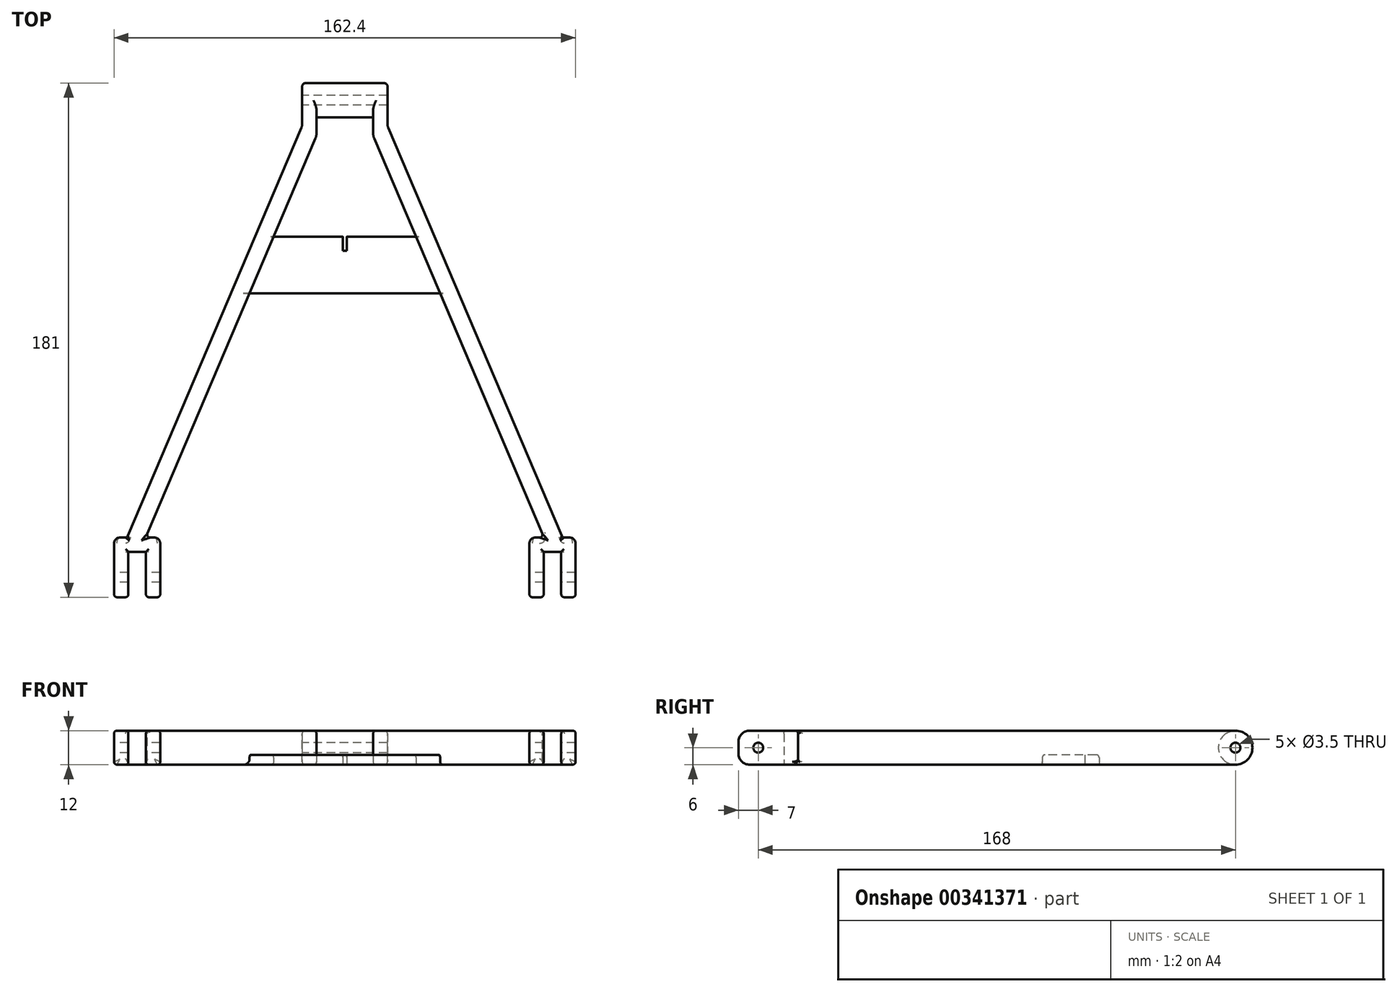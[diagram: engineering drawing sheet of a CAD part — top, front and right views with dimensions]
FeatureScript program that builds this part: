
annotation { "Feature Type Name" : "Feature", "Feature Type Description" : "" }
export const myFeature = defineFeature(function(context is Context, id is Id, definition is map)
    precondition{}
    {
        {
            var Q0;
            Q0=qCreatedBy(makeId("Top.planeOp"),FACE);
            var sketch = newSketch(context, id + "F0", { "sketchPlane" : qUnion([Q0])});
            skLineSegment(sketch, "E0.bottom", {"start": v(-15, 50) * mm, "end": v(-10, 50) * mm});
            skLineSegment(sketch, "E0.left", {"start": v(-15, 50) * mm, "end": v(-15, 35) * mm});
            skLineSegment(sketch, "E0.right", {"start": v(-10, 50) * mm, "end": v(-10, 31.42) * mm});
            skLineSegment(sketch, "E1", {"start": v(-15, 35) * mm, "end": v(-76.6, -110) * mm});
            skLineSegment(sketch, "E2", {"start": v(-10, 31.42) * mm, "end": v(-70.08, -110) * mm});
            skLineSegment(sketch, "E3.bottom", {"start": v(-81.2, -110) * mm, "end": v(-76.6, -110) * mm});
            skLineSegment(sketch, "E3.top", {"start": v(-76.2, -115) * mm, "end": v(-70, -115) * mm});
            skLineSegment(sketch, "E3.left", {"start": v(-81.2, -110) * mm, "end": v(-81.2, -115) * mm});
            skLineSegment(sketch, "E3.right", {"start": v(-65, -110) * mm, "end": v(-65, -115) * mm});
            skLineSegment(sketch, "E4.top", {"start": v(-65, -131) * mm, "end": v(-70, -131) * mm});
            skLineSegment(sketch, "E4.left", {"start": v(-65, -115) * mm, "end": v(-65, -131) * mm});
            skLineSegment(sketch, "E4.right", {"start": v(-70, -115) * mm, "end": v(-70, -131) * mm});
            skLineSegment(sketch, "E5.top", {"start": v(-81.2, -131) * mm, "end": v(-76.2, -131) * mm});
            skLineSegment(sketch, "E5.left", {"start": v(-81.2, -115) * mm, "end": v(-81.2, -131) * mm});
            skLineSegment(sketch, "E5.right", {"start": v(-76.2, -115) * mm, "end": v(-76.2, -131) * mm});
            skPoint(sketch, "E6", {"position": v(-73.1, -110) * mm});
            skLineSegment(sketch, "E7.trimOffspring", {"start": v(-70.08, -110) * mm, "end": v(-65, -110) * mm});
            skPoint(sketch, "E8.visualSharp", {"position": v(-76.6, -110) * mm});
            skPoint(sketch, "E9.visualSharp", {"position": v(-70.08, -110) * mm});
            skPoint(sketch, "E10.visualSharp", {"position": v(-81.2, -110) * mm});
            skPoint(sketch, "E11.visualSharp", {"position": v(-65, -110) * mm});
            skLineSegment(sketch, "E12", {"start": v(-25.05, -4) * mm, "end": v(-0.75, -4) * mm});
            skLineSegment(sketch, "E13", {"start": v(-33.55, -24) * mm, "end": v(0, -24) * mm});
            skLineSegment(sketch, "E14.MirrorCS", {"start": v(70.08, -110) * mm, "end": v(65, -110) * mm});
            skLineSegment(sketch, "E15.MirrorCS", {"start": v(81.2, -110) * mm, "end": v(76.6, -110) * mm});
            skLineSegment(sketch, "E16.MirrorCS", {"start": v(81.2, -110) * mm, "end": v(81.2, -115) * mm});
            skLineSegment(sketch, "E17.MirrorCS", {"start": v(65, -110) * mm, "end": v(65, -115) * mm});
            skLineSegment(sketch, "E18.MirrorCS", {"start": v(76.2, -115) * mm, "end": v(70, -115) * mm});
            skLineSegment(sketch, "E19.MirrorCS", {"start": v(10, 31.42) * mm, "end": v(70.08, -110) * mm});
            skLineSegment(sketch, "E20.MirrorCS", {"start": v(15, 35) * mm, "end": v(76.6, -110) * mm});
            skPoint(sketch, "E21.MirrorP", {"position": v(70.08, -110) * mm});
            skPoint(sketch, "E22.MirrorP", {"position": v(81.2, -110) * mm});
            skPoint(sketch, "E23.MirrorP", {"position": v(76.6, -110) * mm});
            skLineSegment(sketch, "E24.MirrorCS", {"start": v(65, -131) * mm, "end": v(70, -131) * mm});
            skLineSegment(sketch, "E25.MirrorCS", {"start": v(81.2, -115) * mm, "end": v(81.2, -131) * mm});
            skLineSegment(sketch, "E26.MirrorCS", {"start": v(76.2, -115) * mm, "end": v(76.2, -131) * mm});
            skLineSegment(sketch, "E27.MirrorCS", {"start": v(81.2, -131) * mm, "end": v(76.2, -131) * mm});
            skPoint(sketch, "E28.MirrorP", {"position": v(65, -110) * mm});
            skPoint(sketch, "E29.MirrorP", {"position": v(73.1, -110) * mm});
            skLineSegment(sketch, "E30.MirrorCS", {"start": v(70, -115) * mm, "end": v(70, -131) * mm});
            skLineSegment(sketch, "E31.MirrorCS", {"start": v(65, -115) * mm, "end": v(65, -131) * mm});
            skLineSegment(sketch, "E32.MirrorCS", {"start": v(15, 50) * mm, "end": v(15, 35) * mm});
            skLineSegment(sketch, "E33.MirrorCS", {"start": v(15, 50) * mm, "end": v(10, 50) * mm});
            skLineSegment(sketch, "E34.MirrorCS", {"start": v(10, 50) * mm, "end": v(10, 31.42) * mm});
            skLineSegment(sketch, "E35.MirrorCS", {"start": v(33.55, -24) * mm, "end": v(0, -24) * mm});
            skLineSegment(sketch, "E36.MirrorCS", {"start": v(25.05, -4) * mm, "end": v(0.75, -4) * mm});
            skLineSegment(sketch, "E37.top", {"start": v(-0.75, -9) * mm, "end": v(0.75, -9) * mm});
            skLineSegment(sketch, "E37.left", {"start": v(-0.75, -4) * mm, "end": v(-0.75, -9) * mm});
            skLineSegment(sketch, "E37.right", {"start": v(0.75, -4) * mm, "end": v(0.75, -9) * mm});
            skPoint(sketch, "E37.bottom.start.orphan", {"position": v(0, -4) * mm});
            skSolve(sketch);
        }
        {
            var Q0;
            {var subQ3=sQuery(id+"F0.wireOp",EDGE,"E0.top");Q0=makeQuery(id+"F0.imprint","IMPRINT",FACE,{"disambiguationData":[TD([[makeQuery(id+"F0.imprint","IMPRINT",EDGE,{"derivedFrom":subQ3}),-1.0]])]});}
            var Q1;
            Q1=makeQuery(id+"F0.imprint","IMPRINT",FACE,{"disambiguationData":[TD([[makeQuery(id+"F0.imprint","IMPRINT",EDGE,{"derivedFrom":sQuery(id+"F0.wireOp",EDGE,"E0.bottom")}),-1.0]])]});
            var Q2;
            Q2=makeQuery(id+"F0.imprint","IMPRINT",FACE,{"disambiguationData":[TD([[makeQuery(id+"F0.imprint","IMPRINT",EDGE,{"derivedFrom":sQuery(id+"F0.wireOp",EDGE,"c3b13773-6e26-4dbf-9561-b6ef54d447d10.MirrorCS")}),-1.0]])]});
            var Q3;
            Q3=makeQuery(id+"F0.imprint","IMPRINT",FACE,{"disambiguationData":[TD([[makeQuery(id+"F0.imprint","IMPRINT",EDGE,{"derivedFrom":sQuery(id+"F0.wireOp",EDGE,"E14.MirrorCS")}),1.0]])]});
            extrude(context, id + "F1", {"entities" : qUnion([Q0, Q1, Q2, Q3]), "depth" : 12 * mm, "offsetDistance" : 25 * mm});
        }
        {
            var Q0;
            {var subQ4=sQuery(id+"F0.wireOp",EDGE,"E12");Q0=makeQuery(id+"F0.imprint","IMPRINT",FACE,{"disambiguationData":[TD([[makeQuery(id+"F0.imprint","IMPRINT",EDGE,{"derivedFrom":subQ4}),-1.0]])]});}
            extrude(context, id + "F2", {"entities" : qUnion([Q0]), "operationType" : NewBodyOperationType.ADD, "depth" : 3.5 * mm});
        }
        {
            var Q0;
            Q0=makeQuery(id+"F1.opExtrude","SWEPT_FACE",FACE,{"disambiguationData":[OSD([sQuery(id+"F0.wireOp",EDGE,"E0.left")])]});
            var sketch = newSketch(context, id + "F3", { "sketchPlane" : qUnion([Q0])});
            skPoint(sketch, "E38", {"position": v(-50, 6) * mm});
            skCircle(sketch, "E39", {"center": v(-44, 6) * mm, "radius": 6 * mm});
            skSolve(sketch);
        }
        {
            var Q0;
            Q0=qSketchRegion(id+"F3",true);
            var Q1;
            {var subQ0=sQuery(id+"F3.wireOp",EDGE,"E39");var subQ1=sQuery(id+"F0.wireOp",EDGE,"E0.left");var subQ3=makeQuery(id+"F3.imprint","INTERSECT",VERTEX,{"derivedFrom":[makeQuery(id+"F1.opExtrude","CAP_EDGE",EDGE,{"disambiguationData":[OSD([subQ1])],"isStart":false}),subQ0]});Q1=makeQuery(id+"F3.imprint","IMPRINT",FACE,{"disambiguationData":[TD([[makeQuery(id+"F3.imprint","IMPRINT",EDGE,{"disambiguationData":[TD([[subQ3,1.0]])],"derivedFrom":subQ0}),1.0]])]});}
            var Q2;
            Q2=makeQuery(id+"F1.opExtrude","SWEPT_FACE",FACE,{"disambiguationData":[OSD([sQuery(id+"F0.wireOp",EDGE,"E34.MirrorCS")])]});
            extrude(context, id + "F4", {"entities" : qUnion([Q0, Q1]), "operationType" : NewBodyOperationType.ADD, "endBound" : BoundingType.UP_TO_SURFACE, "oppositeDirection" : true, "endBoundEntityFace" : qUnion([Q2]), "depth" : 25 * mm, "offsetDistance" : 25 * mm});
        }
        {
            var Q0;
            {var subQ0=sQuery(id+"F3.wireOp",EDGE,"E39");var subQ1=sQuery(id+"F0.wireOp",EDGE,"E0.left");var subQ4=makeQuery(id+"F1.opExtrude","CAP_EDGE",EDGE,{"disambiguationData":[OSD([subQ1])],"isStart":false});var subQ5=makeQuery(id+"F3.imprint","INTERSECT",VERTEX,{"derivedFrom":[subQ4,subQ0]});Q0=makeQuery(id+"F3.imprint","IMPRINT",FACE,{"disambiguationData":[TD([[makeQuery(id+"F3.imprint","IMPRINT",EDGE,{"disambiguationData":[TD([[subQ5,-1.0]])],"derivedFrom":subQ0}),-1.0]])]});}
            var Q1;
            {var subQ0=sQuery(id+"F3.wireOp",EDGE,"E39");var subQ1=sQuery(id+"F0.wireOp",EDGE,"E0.left");var subQ4=makeQuery(id+"F1.opExtrude","CAP_EDGE",EDGE,{"disambiguationData":[OSD([subQ1])],"isStart":true});var subQ5=makeQuery(id+"F3.imprint","INTERSECT",VERTEX,{"derivedFrom":[subQ4,subQ0]});Q1=makeQuery(id+"F3.imprint","IMPRINT",FACE,{"disambiguationData":[TD([[makeQuery(id+"F3.imprint","IMPRINT",EDGE,{"disambiguationData":[TD([[subQ5,1.0]])],"derivedFrom":subQ0}),-1.0]])]});}
            extrude(context, id + "F5", {"entities" : qUnion([Q0, Q1]), "operationType" : NewBodyOperationType.REMOVE, "oppositeDirection" : true, "depth" : 30 * mm, "offsetDistance" : 25 * mm});
        }
        {
            var Q0;
            Q0=sQuery(id+"F3.wireOp",VERTEX,"E39.center");
            var Q1;
            Q1=makeQuery(id+"F1.opExtrude","SWEPT_BODY",BODY,{"disambiguationData":[OSD([sQuery(id+"F0.wireOp",EDGE,"E0.bottom"),sQuery(id+"F0.wireOp",EDGE,"E0.left"),sQuery(id+"F0.wireOp",EDGE,"E0.right"),sQuery(id+"F0.wireOp",EDGE,"E1"),sQuery(id+"F0.wireOp",EDGE,"E2"),sQuery(id+"F0.wireOp",EDGE,"E3.bottom"),sQuery(id+"F0.wireOp",EDGE,"E3.top"),sQuery(id+"F0.wireOp",EDGE,"E3.left"),sQuery(id+"F0.wireOp",EDGE,"E3.right"),sQuery(id+"F0.wireOp",EDGE,"E4.top"),sQuery(id+"F0.wireOp",EDGE,"E4.left"),sQuery(id+"F0.wireOp",EDGE,"E4.right"),sQuery(id+"F0.wireOp",EDGE,"E5.top"),sQuery(id+"F0.wireOp",EDGE,"E5.left"),sQuery(id+"F0.wireOp",EDGE,"E5.right"),sQuery(id+"F0.wireOp",EDGE,"E7.trimOffspring"),sQuery(id+"F0.wireOp",EDGE,"E8.filletArc"),sQuery(id+"F0.wireOp",EDGE,"E9.filletArc"),sQuery(id+"F0.wireOp",EDGE,"E10.filletArc"),sQuery(id+"F0.wireOp",EDGE,"E11.filletArc")])]});
            hole(context, id + "F6", {"style" : HoleStyle.SIMPLE, "endStyle" : HoleEndStyle.THROUGH, "holeDiameter" : 3.5 * mm, "tappedDepth" : 12 * mm, "tapClearance" : 3, "startFromSketch" : true, "locations" : qUnion([Q0]), "scope" : qUnion([Q1])});
        }
        {
            var Q0;
            Q0=makeQuery(id+"F1.opExtrude","SWEPT_FACE",FACE,{"disambiguationData":[OSD([sQuery(id+"F0.wireOp",EDGE,"E3.left"),sQuery(id+"F0.wireOp",EDGE,"E5.left")])]});
            var sketch = newSketch(context, id + "F7", { "sketchPlane" : qUnion([Q0])});
            skPoint(sketch, "E40", {"position": v(124, 6) * mm});
            skPoint(sketch, "E40.positionSnap0", {"position": v(131, 6) * mm});
            skSolve(sketch);
        }
        {
            var Q0;
            Q0=sQuery(id+"F7.wireOp",VERTEX,"E40");
            var Q1;
            Q1=makeQuery(id+"F1.opExtrude","SWEPT_BODY",BODY,{"disambiguationData":[OSD([sQuery(id+"F0.wireOp",EDGE,"E0.bottom"),sQuery(id+"F0.wireOp",EDGE,"E0.left"),sQuery(id+"F0.wireOp",EDGE,"E0.right"),sQuery(id+"F0.wireOp",EDGE,"E1"),sQuery(id+"F0.wireOp",EDGE,"E2"),sQuery(id+"F0.wireOp",EDGE,"E3.bottom"),sQuery(id+"F0.wireOp",EDGE,"E3.top"),sQuery(id+"F0.wireOp",EDGE,"E3.left"),sQuery(id+"F0.wireOp",EDGE,"E3.right"),sQuery(id+"F0.wireOp",EDGE,"E4.top"),sQuery(id+"F0.wireOp",EDGE,"E4.left"),sQuery(id+"F0.wireOp",EDGE,"E4.right"),sQuery(id+"F0.wireOp",EDGE,"E5.top"),sQuery(id+"F0.wireOp",EDGE,"E5.left"),sQuery(id+"F0.wireOp",EDGE,"E5.right"),sQuery(id+"F0.wireOp",EDGE,"E7.trimOffspring"),sQuery(id+"F0.wireOp",EDGE,"E8.filletArc"),sQuery(id+"F0.wireOp",EDGE,"E9.filletArc"),sQuery(id+"F0.wireOp",EDGE,"E10.filletArc"),sQuery(id+"F0.wireOp",EDGE,"E11.filletArc")])]});
            hole(context, id + "F8", {"style" : HoleStyle.SIMPLE, "endStyle" : HoleEndStyle.THROUGH, "holeDiameter" : 3.5 * mm, "tappedDepth" : 12 * mm, "tapClearance" : 3, "startFromSketch" : true, "locations" : qUnion([Q0]), "scope" : qUnion([Q1])});
        }
        {
            var Q0;
            Q0=makeQuery(id+"F1.opExtrude","CAP_EDGE",EDGE,{"disambiguationData":[OSD([sQuery(id+"F0.wireOp",EDGE,"E27.MirrorCS")])],"isStart":false});
            var Q1;
            Q1=makeQuery(id+"F1.opExtrude","CAP_EDGE",EDGE,{"disambiguationData":[OSD([sQuery(id+"F0.wireOp",EDGE,"E27.MirrorCS")])],"isStart":true});
            var Q2;
            Q2=makeQuery(id+"F1.opExtrude","CAP_EDGE",EDGE,{"disambiguationData":[OSD([sQuery(id+"F0.wireOp",EDGE,"E24.MirrorCS")])],"isStart":false});
            var Q3;
            Q3=makeQuery(id+"F1.opExtrude","CAP_EDGE",EDGE,{"disambiguationData":[OSD([sQuery(id+"F0.wireOp",EDGE,"E24.MirrorCS")])],"isStart":true});
            var Q4;
            Q4=makeQuery(id+"F1.opExtrude","CAP_EDGE",EDGE,{"disambiguationData":[OSD([sQuery(id+"F0.wireOp",EDGE,"E4.top")])],"isStart":false});
            var Q5;
            Q5=makeQuery(id+"F1.opExtrude","CAP_EDGE",EDGE,{"disambiguationData":[OSD([sQuery(id+"F0.wireOp",EDGE,"E4.top")])],"isStart":true});
            var Q6;
            Q6=makeQuery(id+"F1.opExtrude","CAP_EDGE",EDGE,{"disambiguationData":[OSD([sQuery(id+"F0.wireOp",EDGE,"E5.top")])],"isStart":true});
            var Q7;
            Q7=makeQuery(id+"F1.opExtrude","CAP_EDGE",EDGE,{"disambiguationData":[OSD([sQuery(id+"F0.wireOp",EDGE,"E5.top")])],"isStart":false});
            var Q8;
            Q8=makeQuery(id+"F2.opExtrude","SWEPT_EDGE",EDGE,{"disambiguationData":[OSD([sQuery(id+"F0.wireOp",EDGE,"E2"),sQuery(id+"F0.wireOp",EDGE,"E13")])]});
            var Q9;
            Q9=makeQuery(id+"F2.opExtrude","SWEPT_EDGE",EDGE,{"disambiguationData":[OSD([sQuery(id+"F0.wireOp",EDGE,"E19.MirrorCS"),sQuery(id+"F0.wireOp",EDGE,"E35.MirrorCS")])]});
            var Q10;
            Q10=makeQuery(id+"F2.opExtrude","SWEPT_EDGE",EDGE,{"disambiguationData":[OSD([sQuery(id+"F0.wireOp",EDGE,"E2"),sQuery(id+"F0.wireOp",EDGE,"E12")])]});
            var Q11;
            Q11=makeQuery(id+"F2.opExtrude","SWEPT_EDGE",EDGE,{"disambiguationData":[OSD([sQuery(id+"F0.wireOp",EDGE,"E19.MirrorCS"),sQuery(id+"F0.wireOp",EDGE,"E36.MirrorCS")])]});
            var Q12;
            Q12=makeQuery(id+"F2.opExtrude","CAP_EDGE",EDGE,{"disambiguationData":[OSD([sQuery(id+"F0.wireOp",EDGE,"E2")])],"isStart":false});
            var Q13;
            Q13=makeQuery(id+"F2.opExtrude","CAP_EDGE",EDGE,{"disambiguationData":[OSD([sQuery(id+"F0.wireOp",EDGE,"E19.MirrorCS")])],"isStart":false});
            var Q14;
            Q14=makeQuery(id+"F1.opExtrude","SWEPT_EDGE",EDGE,{"disambiguationData":[OSD([sQuery(id+"F0.wireOp",EDGE,"E19.MirrorCS"),sQuery(id+"F0.wireOp",EDGE,"E34.MirrorCS")])]});
            var Q15;
            Q15=makeQuery(id+"F1.opExtrude","SWEPT_EDGE",EDGE,{"disambiguationData":[OSD([sQuery(id+"F0.wireOp",EDGE,"E0.right"),sQuery(id+"F0.wireOp",EDGE,"E2")])]});
            var Q16;
            Q16=makeQuery(id+"F1.opExtrude","SWEPT_EDGE",EDGE,{"disambiguationData":[OSD([sQuery(id+"F0.wireOp",EDGE,"E0.left"),sQuery(id+"F0.wireOp",EDGE,"E1")])]});
            var Q17;
            Q17=makeQuery(id+"F1.opExtrude","SWEPT_EDGE",EDGE,{"disambiguationData":[OSD([sQuery(id+"F0.wireOp",EDGE,"E20.MirrorCS"),sQuery(id+"F0.wireOp",EDGE,"E32.MirrorCS")])]});
            fillet(context, id + "F9", {"entities" : qUnion([Q0, Q1, Q2, Q3, Q4, Q5, Q6, Q7, Q8, Q9, Q10, Q11, Q12, Q13, Q14, Q15, Q16, Q17]), "radius" : 4 * mm, "tangentPropagation" : true, "allowEdgeOverflow" : false});
        }
        {
            var Q0;
            Q0=makeQuery(id+"F1.opExtrude","CAP_FACE",FACE,{"disambiguationData":[OSD([sQuery(id+"F0.wireOp",EDGE,"E14.MirrorCS"),sQuery(id+"F0.wireOp",EDGE,"E15.MirrorCS"),sQuery(id+"F0.wireOp",EDGE,"E16.MirrorCS"),sQuery(id+"F0.wireOp",EDGE,"E17.MirrorCS"),sQuery(id+"F0.wireOp",EDGE,"9b0a4e4a-d26e-4688-b8e9-a85a47df65b34.MirrorCS"),sQuery(id+"F0.wireOp",EDGE,"9b0a4e4a-d26e-4688-b8e9-a85a47df65b35.MirrorCS"),sQuery(id+"F0.wireOp",EDGE,"9b0a4e4a-d26e-4688-b8e9-a85a47df65b36.MirrorCS"),sQuery(id+"F0.wireOp",EDGE,"9b0a4e4a-d26e-4688-b8e9-a85a47df65b37.MirrorCS"),sQuery(id+"F0.wireOp",EDGE,"E18.MirrorCS"),sQuery(id+"F0.wireOp",EDGE,"E19.MirrorCS"),sQuery(id+"F0.wireOp",EDGE,"E20.MirrorCS"),sQuery(id+"F0.wireOp",EDGE,"E24.MirrorCS"),sQuery(id+"F0.wireOp",EDGE,"E25.MirrorCS"),sQuery(id+"F0.wireOp",EDGE,"E26.MirrorCS"),sQuery(id+"F0.wireOp",EDGE,"E27.MirrorCS"),sQuery(id+"F0.wireOp",EDGE,"E30.MirrorCS"),sQuery(id+"F0.wireOp",EDGE,"E31.MirrorCS"),sQuery(id+"F0.wireOp",EDGE,"E32.MirrorCS"),sQuery(id+"F0.wireOp",EDGE,"E33.MirrorCS"),sQuery(id+"F0.wireOp",EDGE,"E34.MirrorCS")])],"isStart":false});
            var Q1;
            Q1=makeQuery(id+"F1.opExtrude","CAP_FACE",FACE,{"disambiguationData":[OSD([sQuery(id+"F0.wireOp",EDGE,"E0.bottom"),sQuery(id+"F0.wireOp",EDGE,"E0.left"),sQuery(id+"F0.wireOp",EDGE,"E0.right"),sQuery(id+"F0.wireOp",EDGE,"E1"),sQuery(id+"F0.wireOp",EDGE,"E2"),sQuery(id+"F0.wireOp",EDGE,"E3.bottom"),sQuery(id+"F0.wireOp",EDGE,"E3.top"),sQuery(id+"F0.wireOp",EDGE,"E3.left"),sQuery(id+"F0.wireOp",EDGE,"E3.right"),sQuery(id+"F0.wireOp",EDGE,"E4.top"),sQuery(id+"F0.wireOp",EDGE,"E4.left"),sQuery(id+"F0.wireOp",EDGE,"E4.right"),sQuery(id+"F0.wireOp",EDGE,"E5.top"),sQuery(id+"F0.wireOp",EDGE,"E5.left"),sQuery(id+"F0.wireOp",EDGE,"E5.right"),sQuery(id+"F0.wireOp",EDGE,"E7.trimOffspring"),sQuery(id+"F0.wireOp",EDGE,"E8.filletArc"),sQuery(id+"F0.wireOp",EDGE,"E9.filletArc"),sQuery(id+"F0.wireOp",EDGE,"E10.filletArc"),sQuery(id+"F0.wireOp",EDGE,"E11.filletArc")])],"isStart":false});
            var Q2;
            Q2=makeQuery(id+"F2.opExtrude","CAP_EDGE",EDGE,{"disambiguationData":[OSD([sQuery(id+"F0.wireOp",EDGE,"E13"),sQuery(id+"F0.wireOp",EDGE,"E35.MirrorCS")])],"isStart":false});
            var Q3;
            Q3=makeQuery(id+"F2.opExtrude","CAP_EDGE",EDGE,{"disambiguationData":[OSD([sQuery(id+"F0.wireOp",EDGE,"E12")])],"isStart":false});
            var Q4;
            Q4=makeQuery(id+"F2.opExtrude","CAP_EDGE",EDGE,{"disambiguationData":[OSD([sQuery(id+"F0.wireOp",EDGE,"E36.MirrorCS")])],"isStart":false});
            var Q5;
            {var subQ0=sQuery(id+"F0.wireOp",EDGE,"E34.MirrorCS");var subQ1=sQuery(id+"F0.wireOp",EDGE,"E19.MirrorCS");Q5=makeQuery(id+"F2.boolean.opBoolean","SPLIT",EDGE,{"disambiguationData":[TD([makeQuery(id+"F1.opExtrude","SWEPT_FACE",FACE,{"disambiguationData":[OSD([subQ0])]})])],"derivedFrom":makeQuery(id+"F1.opExtrude","CAP_EDGE",EDGE,{"disambiguationData":[OSD([subQ1])],"isStart":true})});}
            var Q6;
            {var subQ0=sQuery(id+"F0.wireOp",EDGE,"E0.right");var subQ2=sQuery(id+"F0.wireOp",EDGE,"E2");Q6=makeQuery(id+"F2.boolean.opBoolean","SPLIT",EDGE,{"disambiguationData":[TD([makeQuery(id+"F1.opExtrude","SWEPT_FACE",FACE,{"disambiguationData":[OSD([subQ0])]})])],"derivedFrom":makeQuery(id+"F1.opExtrude","CAP_EDGE",EDGE,{"disambiguationData":[OSD([subQ2])],"isStart":true})});}
            var Q7;
            {var subQ0=sQuery(id+"F0.wireOp",EDGE,"E19.MirrorCS");var subQ2=sQuery(id+"F0.wireOp",EDGE,"E14.MirrorCS");Q7=makeQuery(id+"F2.boolean.opBoolean","SPLIT",EDGE,{"disambiguationData":[TD([makeQuery(id+"F1.opExtrude","SWEPT_FACE",FACE,{"disambiguationData":[OSD([subQ2])]})])],"derivedFrom":makeQuery(id+"F1.opExtrude","CAP_EDGE",EDGE,{"disambiguationData":[OSD([subQ0])],"isStart":true})});}
            fillet(context, id + "F10", {"entities" : qUnion([Q0, Q1, Q2, Q3, Q4, Q5, Q6, Q7]), "radius" : 1 * mm, "tangentPropagation" : true, "allowEdgeOverflow" : false});
        }
        {
            var Q0;
            Q0=makeQuery(id+"F1.opExtrude","SWEPT_EDGE",EDGE,{"disambiguationData":[OSD([sQuery(id+"F0.wireOp",EDGE,"E2"),sQuery(id+"F0.wireOp",EDGE,"E7.trimOffspring")])]});
            var Q1;
            Q1=makeQuery(id+"F1.opExtrude","SWEPT_EDGE",EDGE,{"disambiguationData":[OSD([sQuery(id+"F0.wireOp",EDGE,"E1"),sQuery(id+"F0.wireOp",EDGE,"E3.bottom")])]});
            var Q2;
            Q2=makeQuery(id+"F1.opExtrude","SWEPT_EDGE",EDGE,{"disambiguationData":[OSD([sQuery(id+"F0.wireOp",EDGE,"E14.MirrorCS"),sQuery(id+"F0.wireOp",EDGE,"E19.MirrorCS")])]});
            var Q3;
            Q3=makeQuery(id+"F1.opExtrude","SWEPT_EDGE",EDGE,{"disambiguationData":[OSD([sQuery(id+"F0.wireOp",EDGE,"E15.MirrorCS"),sQuery(id+"F0.wireOp",EDGE,"E20.MirrorCS")])]});
            fillet(context, id + "F11", {"entities" : qUnion([Q0, Q1, Q2, Q3]), "radius" : 1 * mm, "tangentPropagation" : true, "allowEdgeOverflow" : false});
        }
        {
            var Q0;
            Q0=makeQuery(id+"F1.opExtrude","SWEPT_EDGE",EDGE,{"disambiguationData":[OSD([sQuery(id+"F0.wireOp",EDGE,"E15.MirrorCS"),sQuery(id+"F0.wireOp",EDGE,"E16.MirrorCS")])]});
            var Q1;
            Q1=makeQuery(id+"F1.opExtrude","SWEPT_EDGE",EDGE,{"disambiguationData":[OSD([sQuery(id+"F0.wireOp",EDGE,"E3.bottom"),sQuery(id+"F0.wireOp",EDGE,"E3.left")])]});
            var Q2;
            Q2=makeQuery(id+"F1.opExtrude","SWEPT_EDGE",EDGE,{"disambiguationData":[OSD([sQuery(id+"F0.wireOp",EDGE,"E14.MirrorCS"),sQuery(id+"F0.wireOp",EDGE,"E17.MirrorCS")])]});
            var Q3;
            Q3=makeQuery(id+"F1.opExtrude","SWEPT_EDGE",EDGE,{"disambiguationData":[OSD([sQuery(id+"F0.wireOp",EDGE,"E3.right"),sQuery(id+"F0.wireOp",EDGE,"E7.trimOffspring")])]});
            fillet(context, id + "F12", {"entities" : qUnion([Q0, Q1, Q2, Q3]), "radius" : 2 * mm, "tangentPropagation" : true, "allowEdgeOverflow" : false});
        }
    });
